# Revit family: Bathtub_Wall_Set-American_Standard-Studio-2946.BW_Series
name_source: partatom
category: Specialty Equipment
units: mm (PartAtom-declared; Revit-internal decimal feet)

## family parameters
Always vertical = No
Cut with Voids When Loaded = No
OmniClass Number = 23.45.05.14.11.14
OmniClass Title = Bath Panels
Part Type = Normal
Room Calculation Point = No
Round Connector Dimension = Use Diameter
Shared = Yes
Work Plane-Based = Yes

## types (1)
- 2946BW.011
    Assembly Code = D2010710
    Default Elevation = 0"
    Description = Studio 60"x 32" Bath Wall Set
    Door Opening Length = 30 7/8"
    Finish = High Gloss Acrylic-American Standard-011-Arctic
    Height = 58"
    IAPMO Compliance = Meets or Exceeds ANSI Z124.1.2
    Installation Type = Wall Mounted
    Length = 60"
    Manufacturer = American Standard
    Material = High Gloss Acrylic-American Standard-011-Arctic
    Model = 2946BW.011
    Product Documentation Link = https://americanstandard.box.com
    Product Page URL = https://www.americanstandard-us.com
    Revised Date = 01/26/2022
    URL = http://www.americanstandard-us.com
    Warranty Information = Limited Lifetime warranty
    Width = 32"
    cUPC Compliant = Yes

## geometry (parser evidence)
native form markers: Sweep x2
no freeform markers — native parametric forms only
